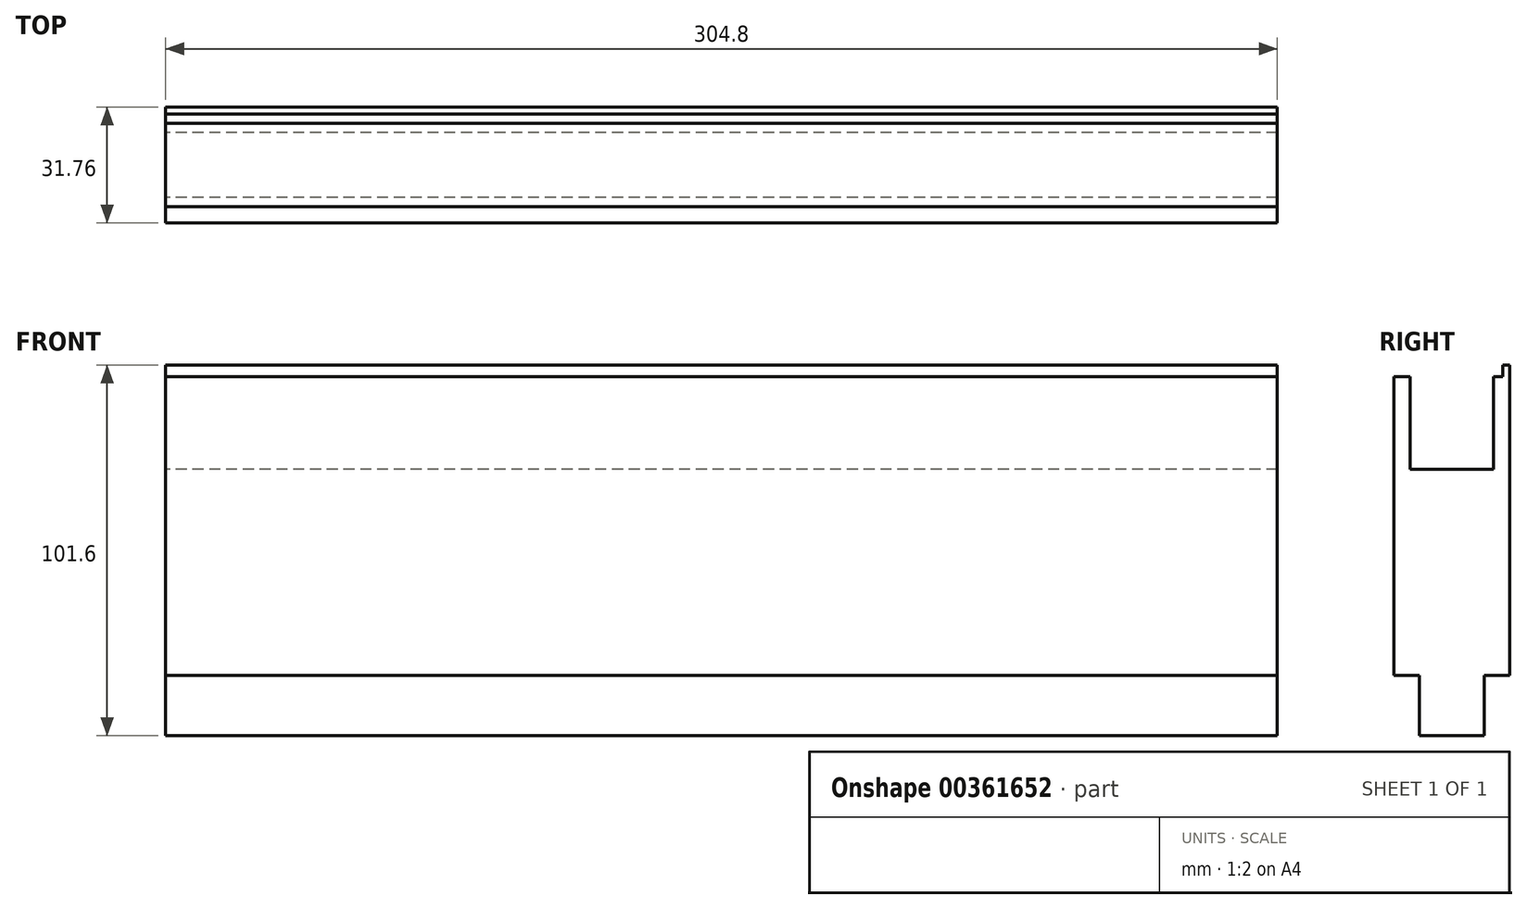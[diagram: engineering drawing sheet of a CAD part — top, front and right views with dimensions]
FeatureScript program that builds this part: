
annotation { "Feature Type Name" : "Feature", "Feature Type Description" : "" }
export const myFeature = defineFeature(function(context is Context, id is Id, definition is map)
    precondition{}
    {
        {
            var Q0;
            Q0=qCreatedBy(makeId("Right.planeOp"),FACE);
            var sketch = newSketch(context, id + "F0", { "sketchPlane" : qUnion([Q0])});
            skLineSegment(sketch, "E0", {"start": v(-15.88, 59.45) * mm, "end": v(-15.87, -22.46) * mm});
            skLineSegment(sketch, "E1", {"start": v(-15.87, -22.46) * mm, "end": v(-8.9, -22.46) * mm});
            skLineSegment(sketch, "E2", {"start": v(-8.9, -22.46) * mm, "end": v(-8.89, -38.97) * mm});
            skLineSegment(sketch, "E3", {"start": v(-8.89, -38.97) * mm, "end": v(8.9, -38.97) * mm});
            skLineSegment(sketch, "E4", {"start": v(8.9, -38.97) * mm, "end": v(8.9, -22.46) * mm});
            skLineSegment(sketch, "E5", {"start": v(8.9, -22.46) * mm, "end": v(15.88, -22.46) * mm});
            skLineSegment(sketch, "E6", {"start": v(15.88, -22.46) * mm, "end": v(15.87, 62.63) * mm});
            skLineSegment(sketch, "E7", {"start": v(13.97, 59.45) * mm, "end": v(13.97, 59.45) * mm});
            skLineSegment(sketch, "E8", {"start": v(13.97, 59.45) * mm, "end": v(11.43, 59.45) * mm});
            skLineSegment(sketch, "E9", {"start": v(11.43, 59.45) * mm, "end": v(11.43, 34.05) * mm});
            skLineSegment(sketch, "E10", {"start": v(11.43, 34.05) * mm, "end": v(-11.43, 34.05) * mm});
            skLineSegment(sketch, "E11", {"start": v(-11.43, 34.05) * mm, "end": v(-11.43, 59.45) * mm});
            skLineSegment(sketch, "E12", {"start": v(-11.43, 59.45) * mm, "end": v(-15.88, 59.45) * mm});
            skLineSegment(sketch, "E13", {"start": v(15.87, 62.63) * mm, "end": v(15.87, 62.63) * mm});
            skLineSegment(sketch, "E14", {"start": v(15.87, 62.63) * mm, "end": v(13.97, 62.63) * mm});
            skLineSegment(sketch, "E15", {"start": v(13.97, 62.63) * mm, "end": v(13.97, 59.45) * mm});
            skSolve(sketch);
        }
        {
            var Q0;
            Q0=makeQuery(id+"F0.imprint","IMPRINT",FACE,{"disambiguationData":[TD([[makeQuery(id+"F0.imprint","IMPRINT",EDGE,{"derivedFrom":sQuery(id+"F0.wireOp",EDGE,"E0")}),1.0]])]});
            extrude(context, id + "F1", {"entities" : qUnion([Q0]), "depth" : 304.8 * mm});
        }
    });
